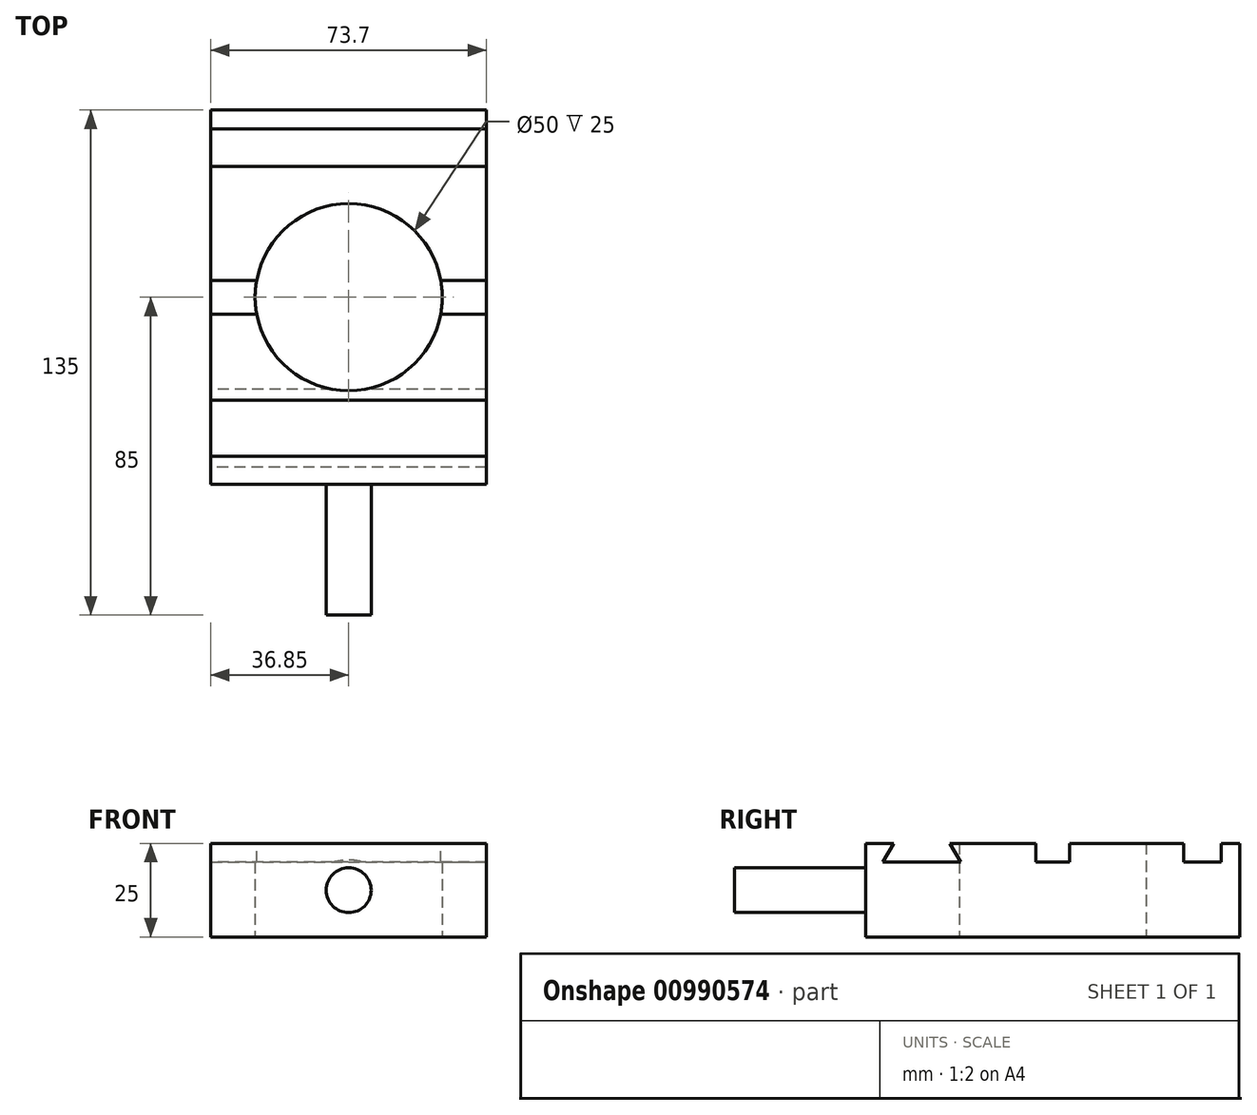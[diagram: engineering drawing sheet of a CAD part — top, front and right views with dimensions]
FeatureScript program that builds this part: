
annotation { "Feature Type Name" : "Feature", "Feature Type Description" : "" }
export const myFeature = defineFeature(function(context is Context, id is Id, definition is map)
    precondition{}
    {
        {
            var Q0;
            Q0=qCreatedBy(makeId("Top.planeOp"),FACE);
            var sketch = newSketch(context, id + "F0", { "sketchPlane" : qUnion([Q0])});
            skLineSegment(sketch, "E0.bottom", {"start": v(36.85, 50) * mm, "end": v(-36.85, 50) * mm});
            skLineSegment(sketch, "E0.top", {"start": v(36.85, -50) * mm, "end": v(-36.85, -50) * mm});
            skLineSegment(sketch, "E0.left", {"start": v(36.85, 50) * mm, "end": v(36.85, -50) * mm});
            skLineSegment(sketch, "E0.right", {"start": v(-36.85, 50) * mm, "end": v(-36.85, -50) * mm});
            skPoint(sketch, "E0.middle", {"position": v(0, 0) * mm});
            skSolve(sketch);
        }
        {
            var Q0;
            Q0=makeQuery(id+"F0.imprint","IMPRINT",FACE,{"disambiguationData":[TD([[makeQuery(id+"F0.imprint","IMPRINT",EDGE,{"derivedFrom":sQuery(id+"F0.wireOp",EDGE,"E0.bottom")}),1.0]])]});
            var sketch = newSketch(context, id + "F1", { "sketchPlane" : qUnion([Q0])});
            skCircle(sketch, "E1", {"center": v(0, 0) * mm, "radius": 25 * mm});
            skSolve(sketch);
        }
        {
            var Q0;
            Q0=makeQuery(id+"F1.imprint","IMPRINT",FACE,{"disambiguationData":[TD([[makeQuery(id+"F1.imprint","IMPRINT",EDGE,{"derivedFrom":sQuery(id+"F1.wireOp",EDGE,"E1")}),-1.0]])]});
            extrude(context, id + "F2", {"entities" : qUnion([Q0]), "depth" : 100 * mm, "offsetDistance" : 25.4 * mm});
        }
        {
            var Q0;
            Q0=makeQuery(id+"F2.opExtrude","CAP_FACE",FACE,{"disambiguationData":[OSD([sQuery(id+"F0.wireOp",EDGE,"E0.bottom"),sQuery(id+"F0.wireOp",EDGE,"E0.top"),sQuery(id+"F0.wireOp",EDGE,"E0.left"),sQuery(id+"F0.wireOp",EDGE,"E0.right"),sQuery(id+"F1.wireOp",EDGE,"E1")])],"isStart":false});
            var sketch = newSketch(context, id + "F3", { "sketchPlane" : qUnion([Q0])});
            skLineSegment(sketch, "E2.bottom", {"start": v(-36.85, 45) * mm, "end": v(36.85, 45) * mm});
            skLineSegment(sketch, "E2.top", {"start": v(-36.85, 35) * mm, "end": v(36.85, 35) * mm});
            skLineSegment(sketch, "E2.left", {"start": v(-36.85, 45) * mm, "end": v(-36.85, 35) * mm});
            skLineSegment(sketch, "E2.right", {"start": v(36.85, 45) * mm, "end": v(36.85, 35) * mm});
            skLineSegment(sketch, "E3", {"start": v(-36.85, 4.5) * mm, "end": v(36.85, 4.5) * mm});
            skLineSegment(sketch, "E4", {"start": v(-36.85, -4.5) * mm, "end": v(36.85, -4.5) * mm});
            skLineSegment(sketch, "E5", {"start": v(36.85, 4.5) * mm, "end": v(36.85, -4.5) * mm});
            skLineSegment(sketch, "E6", {"start": v(-36.85, 4.5) * mm, "end": v(-36.85, -4.5) * mm});
            skPoint(sketch, "E7", {"position": v(0, 0) * mm});
            skLineSegment(sketch, "E8", {"start": v(-36.85, 0) * mm, "end": v(36.85, 0) * mm, "construction": true});
            skSolve(sketch);
        }
        {
            var Q0;
            {var subQ0=sQuery(id+"F3.wireOp",EDGE,"E6");Q0=makeQuery(id+"F3.imprint","IMPRINT",FACE,{"disambiguationData":[TD([[makeQuery(id+"F3.imprint","IMPRINT",EDGE,{"derivedFrom":subQ0}),1.0]])]});}
            var Q1;
            {var subQ0=sQuery(id+"F3.wireOp",EDGE,"E5");Q1=makeQuery(id+"F3.imprint","IMPRINT",FACE,{"disambiguationData":[TD([[makeQuery(id+"F3.imprint","IMPRINT",EDGE,{"derivedFrom":subQ0}),-1.0]])]});}
            var Q2;
            Q2=makeQuery(id+"F3.imprint","IMPRINT",FACE,{"disambiguationData":[TD([[makeQuery(id+"F3.imprint","IMPRINT",EDGE,{"derivedFrom":sQuery(id+"F3.wireOp",EDGE,"E2.bottom")}),-1.0]])]});
            extrude(context, id + "F4", {"entities" : qUnion([Q0, Q1, Q2]), "operationType" : NewBodyOperationType.REMOVE, "oppositeDirection" : true, "depth" : 5 * mm, "offsetDistance" : 25 * mm});
        }
        {
            var Q0;
            Q0=makeQuery(id+"F2.opExtrude","SWEPT_FACE",FACE,{"disambiguationData":[OSD([sQuery(id+"F0.wireOp",EDGE,"E0.right")])]});
            var sketch = newSketch(context, id + "F5", { "sketchPlane" : qUnion([Q0])});
            skLineSegment(sketch, "E9", {"start": v(27.5, 100) * mm, "end": v(24.61, 95) * mm});
            skLineSegment(sketch, "E10", {"start": v(24.61, 95) * mm, "end": v(45.39, 95) * mm});
            skLineSegment(sketch, "E11", {"start": v(45.39, 95) * mm, "end": v(42.5, 100) * mm});
            skLineSegment(sketch, "E12", {"start": v(27.5, 100) * mm, "end": v(42.5, 100) * mm});
            skLineSegment(sketch, "E13", {"start": v(35, 95) * mm, "end": v(35, 100) * mm, "construction": true});
            skSolve(sketch);
        }
        {
            var Q0;
            Q0=makeQuery(id+"F5.imprint","IMPRINT",FACE,{"disambiguationData":[TD([[makeQuery(id+"F5.imprint","IMPRINT",EDGE,{"derivedFrom":sQuery(id+"F5.wireOp",EDGE,"E9")}),1.0]])]});
            var Q1;
            Q1=makeQuery(id+"F2.opExtrude","SWEPT_FACE",FACE,{"disambiguationData":[OSD([sQuery(id+"F0.wireOp",EDGE,"E0.left")])]});
            extrude(context, id + "F6", {"entities" : qUnion([Q0]), "operationType" : NewBodyOperationType.REMOVE, "endBound" : BoundingType.UP_TO_SURFACE, "oppositeDirection" : true, "depth" : 25 * mm, "endBoundEntityFace" : qUnion([Q1]), "offsetDistance" : 25 * mm});
        }
        {
            var Q0;
            Q0=makeQuery(id+"F0.imprint","IMPRINT",FACE,{"disambiguationData":[TD([[makeQuery(id+"F0.imprint","IMPRINT",EDGE,{"derivedFrom":sQuery(id+"F0.wireOp",EDGE,"E0.bottom")}),1.0]])]});
            extrude(context, id + "F7", {"entities" : qUnion([Q0]), "operationType" : NewBodyOperationType.REMOVE, "oppositeDirection" : true, "depth" : 75 * mm, "offsetDistance" : 25 * mm});
        }
        {
            var Q0;
            Q0=makeQuery(id+"F2.opExtrude","CAP_FACE",FACE,{"disambiguationData":[OSD([sQuery(id+"F0.wireOp",EDGE,"E0.bottom"),sQuery(id+"F0.wireOp",EDGE,"E0.top"),sQuery(id+"F0.wireOp",EDGE,"E0.left"),sQuery(id+"F0.wireOp",EDGE,"E0.right"),sQuery(id+"F1.wireOp",EDGE,"E1")])],"isStart":true});
            extrude(context, id + "F8", {"entities" : qUnion([Q0]), "operationType" : NewBodyOperationType.REMOVE, "oppositeDirection" : true, "depth" : 75 * mm, "offsetDistance" : 25 * mm});
        }
        {
            var Q0;
            Q0=makeQuery(id+"F2.opExtrude","SWEPT_FACE",FACE,{"disambiguationData":[OSD([sQuery(id+"F0.wireOp",EDGE,"E0.top")])]});
            var sketch = newSketch(context, id + "F9", { "sketchPlane" : qUnion([Q0])});
            skCircle(sketch, "E14", {"center": v(0, 87.5) * mm, "radius": 6 * mm});
            skPoint(sketch, "E14.centerSnap0", {"position": v(-36.85, 87.5) * mm});
            skPoint(sketch, "E14.centerSnap1", {"position": v(0, 100) * mm});
            skSolve(sketch);
        }
        {
            var Q0;
            Q0=makeQuery(id+"F9.imprint","IMPRINT",FACE,{"disambiguationData":[TD([[makeQuery(id+"F9.imprint","IMPRINT",EDGE,{"derivedFrom":sQuery(id+"F9.wireOp",EDGE,"E14")}),1.0]])]});
            extrude(context, id + "F10", {"entities" : qUnion([Q0]), "operationType" : NewBodyOperationType.ADD, "depth" : 35 * mm, "offsetDistance" : 25 * mm});
        }
    });
